# Revit family: Toilet_Seat-Square_Closed_Front-KOHLER- ESCALE-K-4417IN
name_source: partatom
category: Specialty Equipment
revit_build: Autodesk Revit 2017 (Build: 20160225_1515(x64)
units: mm (PartAtom-declared; Revit-internal decimal feet)

## family parameters
Cut with Voids When Loaded = No
Host = Face
OmniClass Number = 23.31.19.19.17
OmniClass Title = Water Closet Seats
Part Type = Normal
Room Calculation Point = No
Round Connector Dimension = Use Diameter
Shared = No

## types (4) — shared parameters
ADA Compliant = No
Assembly Code = C1030200
Date Modified = 12/22/2020
Default Elevation = 0"
Description = SOFT CLOSE SEAT
Height = 2 15/16"
Length = 18 1/16"
Manufacturer = KOHLER Co.
Master Format 2014 = 10 28 00
Master Format 2014 Name = Toilet, Bath, and Laundry Accessories
Material = Plastic
Product Name = ESCALE
URL = https://www.kohler.co.in
WaterSense Certified = No
Width = 15 5/16"

## per-type parameters (varying)
| type | Finish | Model | Type |
| 0- White | Kohler-Plastic-0-White | K-4417IN-0 | 1 |
| 7-Black black | Kohler-Plastic-7-Black_Black | K-4417IN-7 | 2 |
| PP,0- White | Kohler-Plastic-0-White | K-4417IN-PP-0 | 3 |
| PP, 7- Black black | Kohler-Plastic-7-Black_Black | K-4417IN-PP-7 | 4 |

## geometry (parser evidence)
native form markers: Sweep x5
no freeform markers — native parametric forms only
